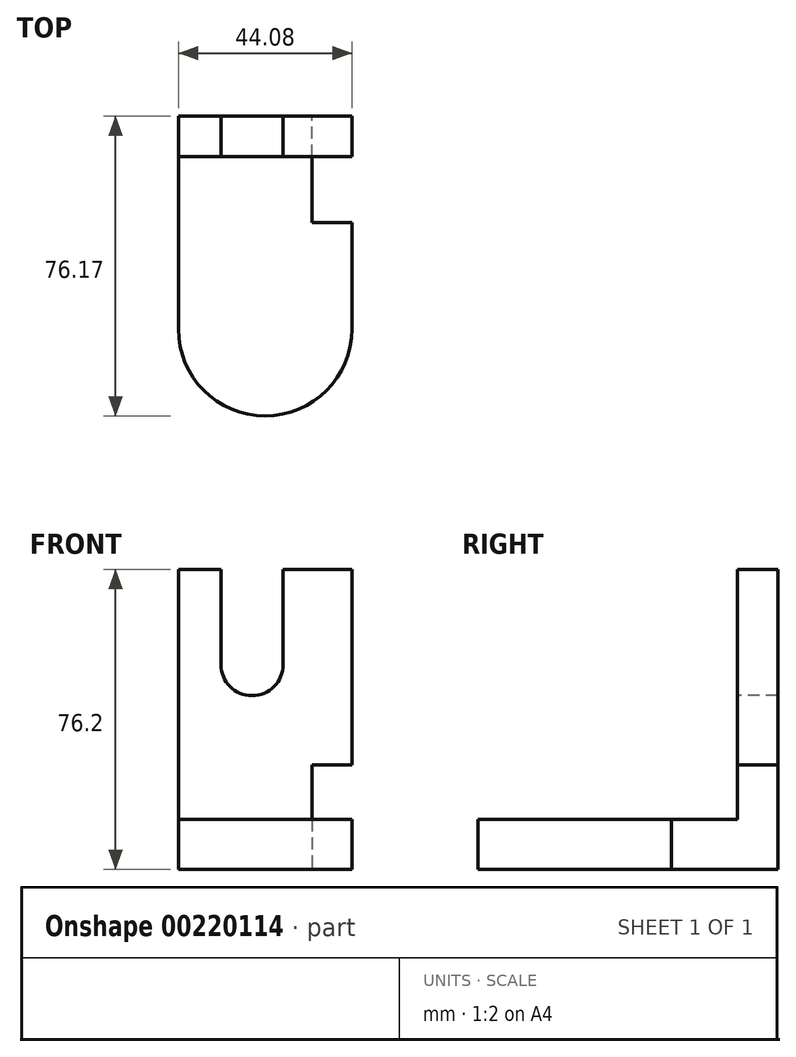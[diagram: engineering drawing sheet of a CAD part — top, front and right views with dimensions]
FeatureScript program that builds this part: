
annotation { "Feature Type Name" : "Feature", "Feature Type Description" : "" }
export const myFeature = defineFeature(function(context is Context, id is Id, definition is map)
    precondition{}
    {
        {
            var Q0;
            Q0=qCreatedBy(makeId("Top.planeOp"),FACE);
            var sketch = newSketch(context, id + "F0", { "sketchPlane" : qUnion([Q0])});
            skLineSegment(sketch, "E0.bottom", {"start": v(22.04, -27.06) * mm, "end": v(-22.04, -27.06) * mm});
            skLineSegment(sketch, "E0.top", {"start": v(22.04, 27.06) * mm, "end": v(-22.04, 27.06) * mm});
            skLineSegment(sketch, "E0.left", {"start": v(22.04, -27.06) * mm, "end": v(22.04, 27.06) * mm});
            skLineSegment(sketch, "E0.right", {"start": v(-22.04, -27.06) * mm, "end": v(-22.04, 27.06) * mm});
            skPoint(sketch, "E0.middle", {"position": v(0, 0) * mm});
            skArc(sketch, "E1", {"start": v(-22.04, -27.06) * mm, "mid": v(0, -49.1) * mm, "end": v(22.04, -27.06) * mm});
            skSolve(sketch);
        }
        {
            var Q0;
            Q0 = qSketchRegion(id + "F0", true);
            extrude(context, id + "F1", {"entities" : qUnion([Q0]), "depth" : 12.7 * mm});
        }
        {
            var Q0;
            Q0=makeQuery(id+"F1.opExtrude","CAP_FACE",FACE,{"disambiguationData":[OSD([sQuery(id+"F0.wireOp",EDGE,"E0.top"),sQuery(id+"F0.wireOp",EDGE,"E0.left"),sQuery(id+"F0.wireOp",EDGE,"E0.right"),sQuery(id+"F0.wireOp",EDGE,"E1")])],"isStart":false});
            var sketch = newSketch(context, id + "F2", { "sketchPlane" : qUnion([Q0])});
            skLineSegment(sketch, "E2.0", {"start": v(22.04, 27.06) * mm, "end": v(-22.04, 27.06) * mm});
            skLineSegment(sketch, "E3.0", {"start": v(22.04, -27.06) * mm, "end": v(22.04, 27.06) * mm});
            skLineSegment(sketch, "E4.0", {"start": v(-22.04, -27.06) * mm, "end": v(-22.04, 27.06) * mm});
            skLineSegment(sketch, "E5", {"start": v(-22.04, 16.79) * mm, "end": v(22.04, 16.79) * mm});
            skSolve(sketch);
        }
        {
            var Q0;
            Q0 = qSketchRegion(id + "F2", true);
            extrude(context, id + "F3", {"entities" : qUnion([Q0]), "operationType" : NewBodyOperationType.ADD, "depth" : 63.5 * mm});
        }
        {
            var Q0;
            Q0=makeQuery(id+"F3.boolean.opBoolean","MERGE",FACE,{"derivedFrom":[makeQuery(id+"F1.opExtrude","SWEPT_FACE",FACE,{"disambiguationData":[OSD([sQuery(id+"F0.wireOp",EDGE,"E0.left")])]}),makeQuery(id+"F3.opExtrude","SWEPT_FACE",FACE,{"disambiguationData":[OSD([sQuery(id+"F2.wireOp",EDGE,"E3.0")])]})]});
            var sketch = newSketch(context, id + "F4", { "sketchPlane" : qUnion([Q0])});
            skLineSegment(sketch, "E6.0", {"start": v(-27.06, 12.7) * mm, "end": v(16.79, 12.7) * mm});
            skLineSegment(sketch, "E7.0", {"start": v(-27.06, 0) * mm, "end": v(27.06, 0) * mm});
            skLineSegment(sketch, "E8.0", {"start": v(27.06, 76.2) * mm, "end": v(27.06, 0) * mm});
            skLineSegment(sketch, "E9.0", {"start": v(16.79, 76.2) * mm, "end": v(16.79, 12.7) * mm});
            skLineSegment(sketch, "E10", {"start": v(0, 12.7) * mm, "end": v(0, 0) * mm});
            skLineSegment(sketch, "E11", {"start": v(0, 0) * mm, "end": v(27.06, 0) * mm});
            skLineSegment(sketch, "E12", {"start": v(16.79, 26.56) * mm, "end": v(27.06, 26.56) * mm});
            skSolve(sketch);
        }
        {
            var Q0;
            Q0 = qSketchRegion(id + "F4", true);
            extrude(context, id + "F5", {"entities" : qUnion([Q0]), "operationType" : NewBodyOperationType.REMOVE, "oppositeDirection" : true, "depth" : 10.16 * mm});
        }
        {
            var Q0;
            Q0=makeQuery(id+"F3.opExtrude","SWEPT_FACE",FACE,{"disambiguationData":[OSD([sQuery(id+"F2.wireOp",EDGE,"E5")])]});
            var sketch = newSketch(context, id + "F6", { "sketchPlane" : qUnion([Q0])});
            skLineSegment(sketch, "E13", {"start": v(-11.24, 76.2) * mm, "end": v(-11.24, 52.02) * mm});
            skLineSegment(sketch, "E14", {"start": v(-11.24, 52.02) * mm, "end": v(4.54, 52.02) * mm});
            skLineSegment(sketch, "E15", {"start": v(4.54, 52.02) * mm, "end": v(4.54, 76.2) * mm});
            skArc(sketch, "E16", {"start": v(-11.24, 52.02) * mm, "mid": v(-3.35, 44.13) * mm, "end": v(4.54, 52.02) * mm});
            skSolve(sketch);
        }
        {
            var Q0;
            Q0 = qSketchRegion(id + "F6", true);
            var Q1;
            {var subQ0=sQuery(id+"F6.wireOp",EDGE,"E13");Q1=makeQuery(id+"F6.imprint","IMPRINT",FACE,{"disambiguationData":[TD([[makeQuery(id+"F6.imprint","IMPRINT",EDGE,{"derivedFrom":subQ0}),1.0]])]});}
            extrude(context, id + "F7", {"entities" : qUnion([Q0, Q1]), "operationType" : NewBodyOperationType.REMOVE, "endBound" : BoundingType.THROUGH_ALL, "oppositeDirection" : true, "depth" : 25.4 * mm});
        }
    });
